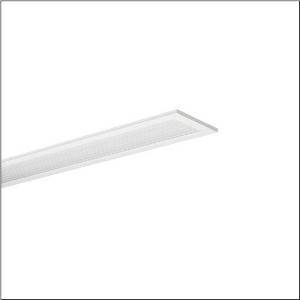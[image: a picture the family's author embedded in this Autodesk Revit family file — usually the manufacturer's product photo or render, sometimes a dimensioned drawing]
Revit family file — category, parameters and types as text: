
# Revit family: apollon_21_linear_51mq15wm2414
name_source: partatom
category: Lighting Fixtures
units: mm (PartAtom-declared; Revit-internal decimal feet)

## family parameters
Cut with Voids When Loaded = No
Host = Face
Light Source = No
Part Type = Normal
Room Calculation Point = No
Round Connector Dimension = Use Diameter
Shared = No

## types (1)
- --- (1 x LED, 4290 lm, 29.7 W, 4000K)
    Apparent Load = 30 VA
    CIE Flux Codes = 66 89 97 100 100
    Color Rendering = 80
    Color Temperature = 4000K
    Default Elevation = 1800 mm
    Description = Apollon 21 linear, office luminaire, primary optical cover: micro prismatic cover, of PMMA, CAT 2 (L<= 3000cd/m²), light emission: direct distribution, primary light characteristic: symmetric, installation type: lay-in mounting, LED, rated luminous flux: 2.540lm, luminous efficacy: 147lm/W, light colour: 840, colour temperature: 4000K, control gear: ON/OFF Multilumen, with terminal, 3-pole, mains connection: 220..240V, AC/DC, 0/50..60Hz, rated input power: 17.3W, housing, of aluminium, coated, traffic white (RAL 9016), length: 1.245mm, width: 179mm, height: 55mm, recess depth: 180mm, housing upper side, of sheet steel, galvanised, protection rating (complete): IP20, protection rating (lamp compartment, on room side): IP50, insulation class (complete): insulation class II (safety insulation), certification: CE, ENEC, impact resistance: IK03, permissible operating ambient temperature: -20..+45°C, permissible storage temperature: -40..+80°C, standard: EN 60598-2-22, packaging unit: 1 piece
    Height = 0 mm  [stored 0 ft]
    Lamp = 1 x LED
    Lamp Light Flux = 4290 lm
    Lamp Power = 29.7 W
    Lamp count = 1
    Length = 1245 mm
    Luminous efficacy = 144 lm/W
    Manufacturer = Siteco
    ModVariant = No
    Model = 51MQ15WM2414
    Mounting Place = Ceiling
    Mounting Type = Recessed
    Number of Poles = 1
    OnlyDefault = Yes
    Power Factor = 1
    Product Name = Apollon 21 linear
    Product group = office luminaire | ceiling recessed
    ProductGroupID = 401
    Protection Class = Protection class II
    Protection Degree = IP 20
    RLX_Detail_Level = 1
    RLX_Emergency_Light_Flux = 0 lm
    RLX_Emergency_Type = 0
    RLX_Emergency_Type_DB = No
    RlxData = <blob elided: 13897 chars, md5=06f031db>
    Socket = socket
    Standby Power = 0 W
    System Light Flux = 4290 lm
    System Power = 30 W
    Type Comments = factory setting: luminous flux: 100 % | (ON | ON | ON) | 700 mA
    Type Image = l_1291018.jpg
    URL = http://relux.com
    VarID = @adj_068358
    Voltage = 0 V
    Weight = 0.00 kg
    Width = 179 mm

note: [stored X ft] marks values corroborated as IEEE doubles in the binary element streams (Revit-internal decimal feet)

## geometry (parser evidence)
native form markers: Sweep x12
no freeform markers — native parametric forms only
